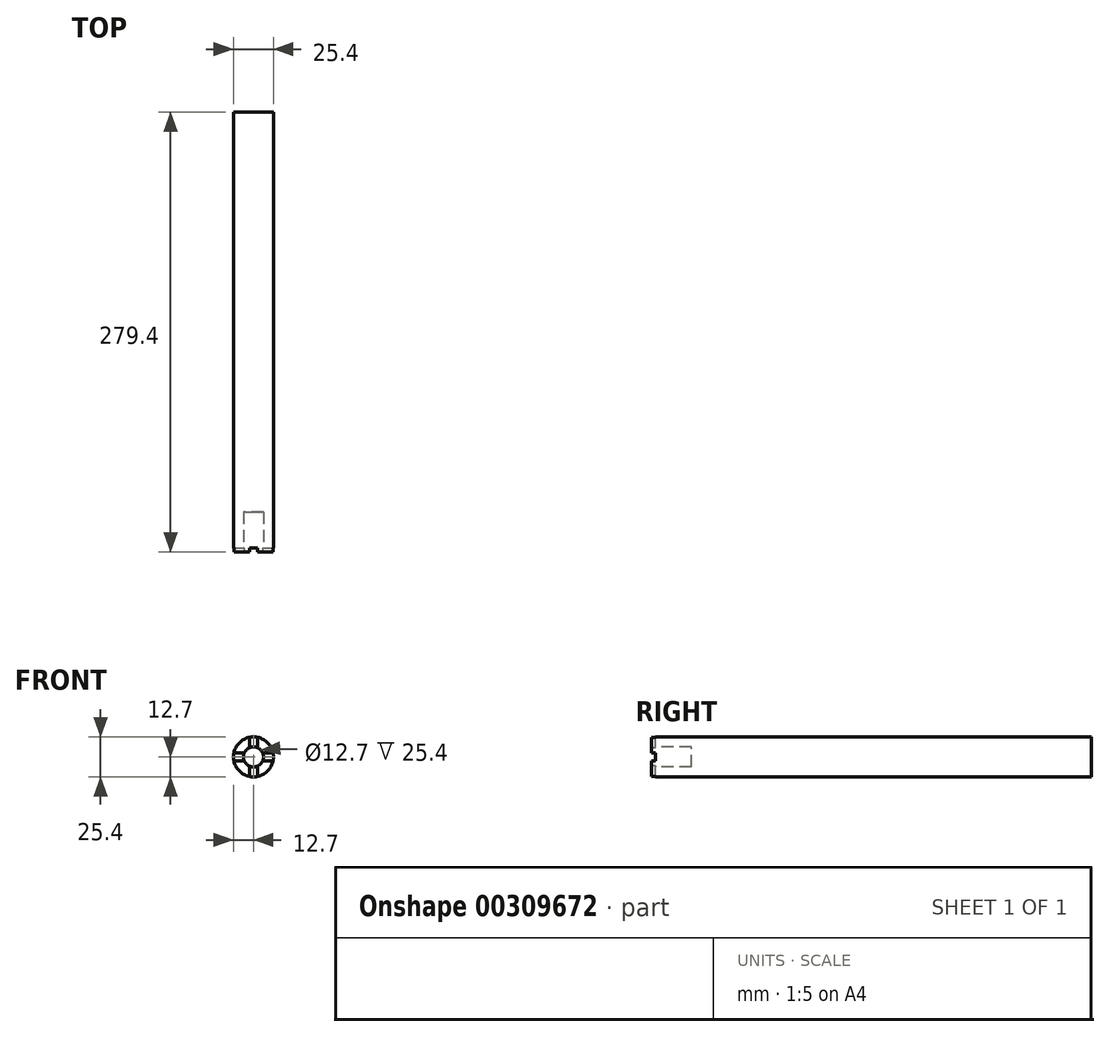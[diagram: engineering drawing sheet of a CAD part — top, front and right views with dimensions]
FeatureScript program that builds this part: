
annotation { "Feature Type Name" : "Feature", "Feature Type Description" : "" }
export const myFeature = defineFeature(function(context is Context, id is Id, definition is map)
    precondition{}
    {
        {
            var Q0;
            Q0=qCreatedBy(makeId("Front.planeOp"),FACE);
            var sketch = newSketch(context, id + "F0", { "sketchPlane" : qUnion([Q0])});
            skCircle(sketch, "E0", {"center": v(0, 0) * mm, "radius": 12.7 * mm});
            skSolve(sketch);
        }
        {
            var Q0;
            Q0 = qSketchRegion(id + "F0", true);
            extrude(context, id + "F1", {"entities" : qUnion([Q0]), "depth" : 279.4 * mm});
        }
        {
            var Q0;
            Q0=makeQuery(id+"F1.opExtrude","CAP_FACE",FACE,{"disambiguationData":[OSD([sQuery(id+"F0.wireOp",EDGE,"E0")])],"isStart":false});
            var sketch = newSketch(context, id + "F2", { "sketchPlane" : qUnion([Q0])});
            skCircle(sketch, "E1", {"center": v(0, 0) * mm, "radius": 6.35 * mm});
            skSolve(sketch);
        }
        {
            var Q0;
            Q0 = qSketchRegion(id + "F2", true);
            extrude(context, id + "F3", {"entities" : qUnion([Q0]), "operationType" : NewBodyOperationType.REMOVE, "oppositeDirection" : true, "depth" : 25.4 * mm});
        }
        {
            var Q0;
            Q0=qCreatedBy(makeId("Top.planeOp"),FACE);
            var sketch = newSketch(context, id + "F4", { "sketchPlane" : qUnion([Q0])});
            skLineSegment(sketch, "E2", {"start": v(0, 0) * mm, "end": v(0, -279.4) * mm, "construction": true});
            skLineSegment(sketch, "E3.bottom", {"start": v(-2.54, -279.4) * mm, "end": v(2.54, -279.4) * mm});
            skLineSegment(sketch, "E3.top", {"start": v(-2.54, -276.86) * mm, "end": v(2.54, -276.86) * mm});
            skLineSegment(sketch, "E3.left", {"start": v(-2.54, -279.4) * mm, "end": v(-2.54, -276.86) * mm});
            skLineSegment(sketch, "E3.right", {"start": v(2.54, -279.4) * mm, "end": v(2.54, -276.86) * mm});
            skSolve(sketch);
        }
        {
            var Q0;
            Q0 = qSketchRegion(id + "F4", true);
            extrude(context, id + "F5", {"entities" : qUnion([Q0]), "operationType" : NewBodyOperationType.REMOVE, "endBound" : BoundingType.THROUGH_ALL, "oppositeDirection" : true, "depth" : 25.4 * mm, "hasSecondDirection" : true, "secondDirectionOppositeDirection" : false, "secondDirectionDepth" : 25.4 * mm});
        }
        {
            var Q0;
            Q0=qCreatedBy(makeId("Right.planeOp"),FACE);
            var sketch = newSketch(context, id + "F6", { "sketchPlane" : qUnion([Q0])});
            skLineSegment(sketch, "E4", {"start": v(0, 0) * mm, "end": v(-279.4, 0) * mm, "construction": true});
            skLineSegment(sketch, "E5.bottom", {"start": v(-279.4, 2.54) * mm, "end": v(-276.86, 2.54) * mm});
            skLineSegment(sketch, "E5.top", {"start": v(-279.4, -2.54) * mm, "end": v(-276.86, -2.54) * mm});
            skLineSegment(sketch, "E5.left", {"start": v(-279.4, 2.54) * mm, "end": v(-279.4, -2.54) * mm});
            skLineSegment(sketch, "E5.right", {"start": v(-276.86, 2.54) * mm, "end": v(-276.86, -2.54) * mm});
            skSolve(sketch);
        }
        {
            var Q0;
            Q0 = qSketchRegion(id + "F6", true);
            extrude(context, id + "F7", {"entities" : qUnion([Q0]), "operationType" : NewBodyOperationType.REMOVE, "endBound" : BoundingType.THROUGH_ALL, "oppositeDirection" : true, "depth" : 25.4 * mm, "hasSecondDirection" : true, "secondDirectionBound" : SecondDirectionBoundingType.THROUGH_ALL, "secondDirectionOppositeDirection" : false, "secondDirectionDepth" : 25.4 * mm});
        }
    });
